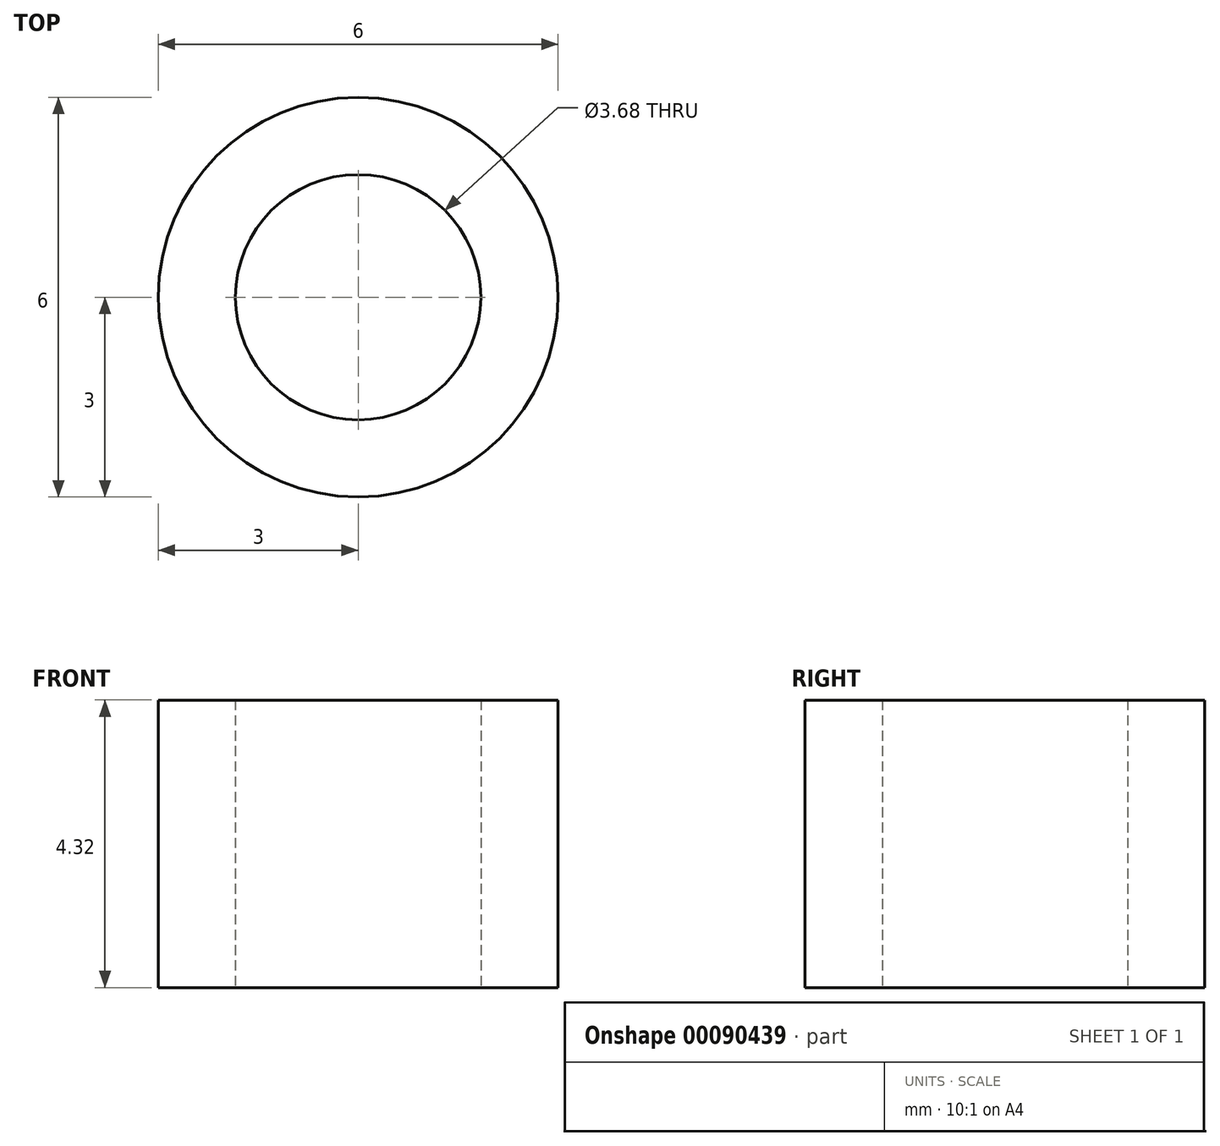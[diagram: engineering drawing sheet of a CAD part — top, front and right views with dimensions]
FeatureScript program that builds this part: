
annotation { "Feature Type Name" : "Feature", "Feature Type Description" : "" }
export const myFeature = defineFeature(function(context is Context, id is Id, definition is map)
    precondition{}
    {
        {
            var Q0;
            Q0=qCreatedBy(makeId("Top.planeOp"),FACE);
            var sketch = newSketch(context, id + "F0", { "sketchPlane" : qUnion([Q0])});
            skCircle(sketch, "E0", {"center": v(0, 0) * mm, "radius": 3 * mm});
            skCircle(sketch, "E1", {"center": v(0, 0) * mm, "radius": 1.84 * mm});
            skSolve(sketch);
        }
        {
            var Q0;
            Q0 = qSketchRegion(id + "F0", true);
            extrude(context, id + "F1", {"entities" : qUnion([Q0]), "depth" : 4.32 * mm});
        }
    });
